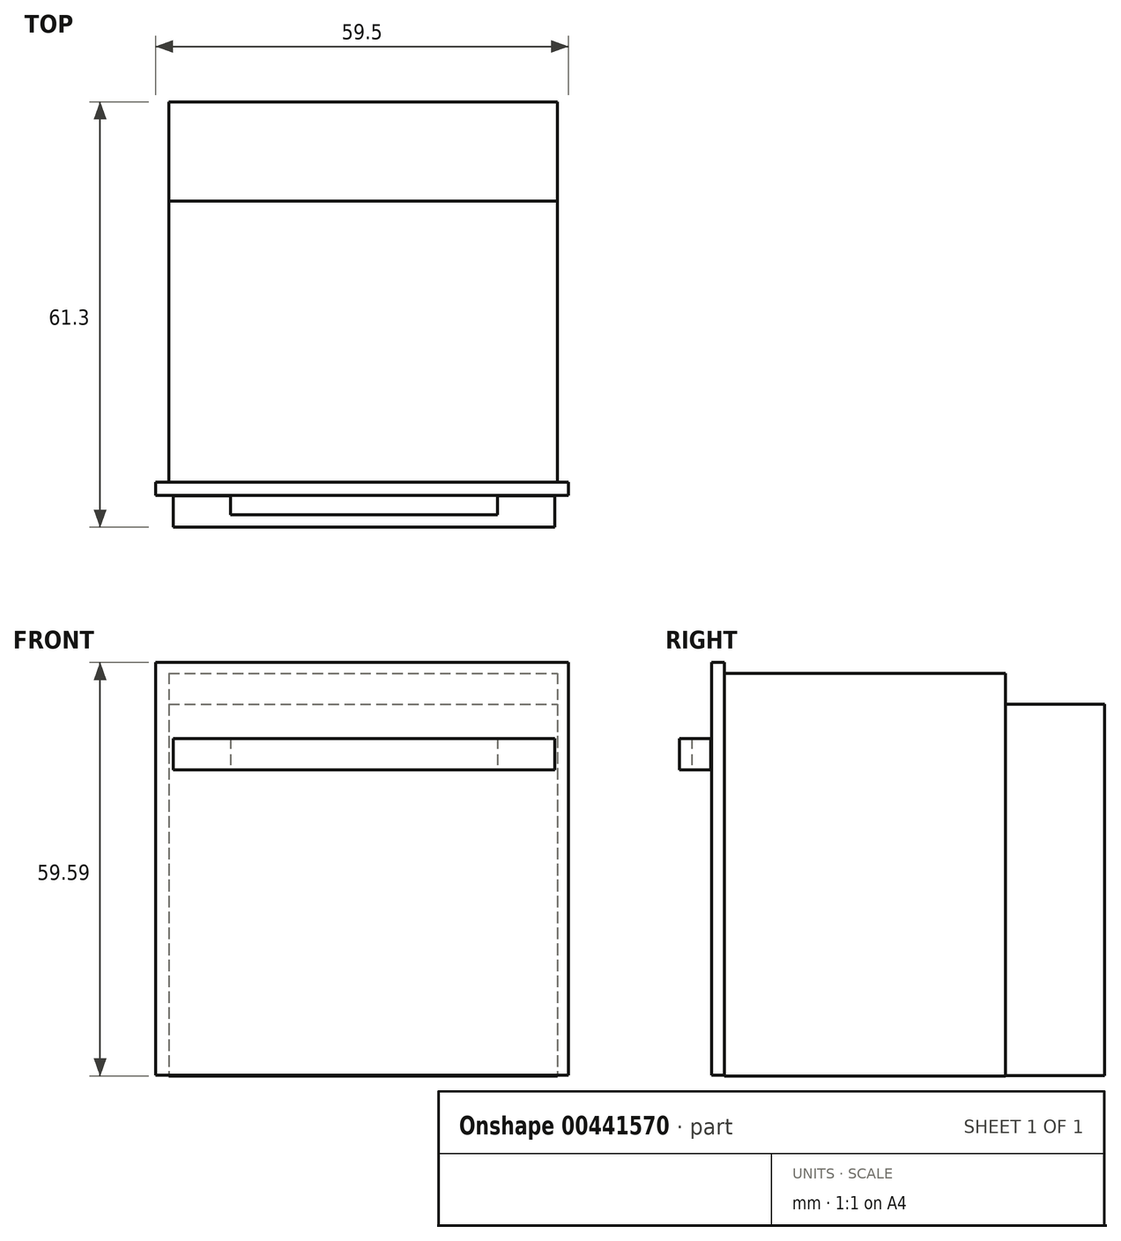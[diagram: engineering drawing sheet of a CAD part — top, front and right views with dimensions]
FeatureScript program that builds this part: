
annotation { "Feature Type Name" : "Feature", "Feature Type Description" : "" }
export const myFeature = defineFeature(function(context is Context, id is Id, definition is map)
    precondition{}
    {
        {
            var Q0;
            Q0=qCreatedBy(makeId("Front.planeOp"),FACE);
            var sketch = newSketch(context, id + "F0", { "sketchPlane" : qUnion([Q0])});
            skLineSegment(sketch, "E0.bottom", {"start": v(-27.15, 28.19) * mm, "end": v(28.85, 28.19) * mm});
            skLineSegment(sketch, "E0.top", {"start": v(-27.15, -29.81) * mm, "end": v(28.85, -29.81) * mm});
            skLineSegment(sketch, "E0.left", {"start": v(-27.15, 28.19) * mm, "end": v(-27.15, -29.81) * mm});
            skLineSegment(sketch, "E0.right", {"start": v(28.85, 28.19) * mm, "end": v(28.85, -29.81) * mm});
            skSolve(sketch);
        }
        {
            var Q0;
            Q0=makeQuery(id+"F0.imprint","IMPRINT",FACE,{"disambiguationData":[TD([[makeQuery(id+"F0.imprint","IMPRINT",EDGE,{"derivedFrom":sQuery(id+"F0.wireOp",EDGE,"E0.bottom")}),-1.0]])]});
            extrude(context, id + "F1", {"entities" : qUnion([Q0]), "depth" : 40.5 * mm});
        }
        {
            var Q0;
            Q0=qCreatedBy(makeId("Front.planeOp"),FACE);
            var sketch = newSketch(context, id + "F2", { "sketchPlane" : qUnion([Q0])});
            skLineSegment(sketch, "E1.bottom", {"start": v(-29.54, 26.56) * mm, "end": v(26.46, 26.56) * mm});
            skLineSegment(sketch, "E1.top", {"start": v(-29.54, -26.94) * mm, "end": v(26.46, -26.94) * mm});
            skLineSegment(sketch, "E1.left", {"start": v(-29.54, 26.56) * mm, "end": v(-29.54, -26.94) * mm});
            skLineSegment(sketch, "E1.right", {"start": v(26.46, 26.56) * mm, "end": v(26.46, -26.94) * mm});
            skSolve(sketch);
        }
        {
            var Q0;
            Q0 = qSketchRegion(id + "F2", true);
            extrude(context, id + "F3", {"entities" : qUnion([Q0]), "depth" : 14.3 * mm});
        }
        {
            var Q0;
            Q0=makeQuery(id+"F3.opExtrude","SWEPT_BODY",BODY,{"disambiguationData":[OSD([sQuery(id+"F2.wireOp",EDGE,"E1.bottom"),sQuery(id+"F2.wireOp",EDGE,"E1.top"),sQuery(id+"F2.wireOp",EDGE,"E1.left"),sQuery(id+"F2.wireOp",EDGE,"E1.right")])]});
            var Q1;
            Q1=makeQuery(id+"F3.opExtrude","CAP_FACE",FACE,{"disambiguationData":[OSD([sQuery(id+"F2.wireOp",EDGE,"E1.bottom"),sQuery(id+"F2.wireOp",EDGE,"E1.top"),sQuery(id+"F2.wireOp",EDGE,"E1.left"),sQuery(id+"F2.wireOp",EDGE,"E1.right")])],"isStart":false});
            transform(context, id + "F4", {"entities" : qUnion([Q0]), "transformType" : TransformType.TRANSLATION_DISTANCE, "transformDirection" : qUnion([Q1]), "distance" : 16.5 * mm, "oppositeDirection" : true, "makeCopy" : false});
        }
        {
            var Q0;
            Q0=makeQuery(id+"F3.opExtrude","SWEPT_BODY",BODY,{"disambiguationData":[OSD([sQuery(id+"F2.wireOp",EDGE,"E1.bottom"),sQuery(id+"F2.wireOp",EDGE,"E1.top"),sQuery(id+"F2.wireOp",EDGE,"E1.left"),sQuery(id+"F2.wireOp",EDGE,"E1.right")])]});
            transform(context, id + "F5", {"entities" : qUnion([Q0]), "transformType" : TransformType.TRANSLATION_3D, "dx" : 2.4 * mm, "dy" : -2.2 * mm, "dz" : -2.8 * mm, "makeCopy" : false});
        }
        {
            var Q0;
            Q0=qCreatedBy(makeId("Front.planeOp"),FACE);
            var sketch = newSketch(context, id + "F6", { "sketchPlane" : qUnion([Q0])});
            skLineSegment(sketch, "E2.bottom", {"start": v(-30.65, 29.85) * mm, "end": v(28.85, 29.85) * mm});
            skLineSegment(sketch, "E2.top", {"start": v(-30.65, -29.65) * mm, "end": v(28.85, -29.65) * mm});
            skLineSegment(sketch, "E2.left", {"start": v(-30.65, 29.85) * mm, "end": v(-30.65, -29.65) * mm});
            skLineSegment(sketch, "E2.right", {"start": v(28.85, 29.85) * mm, "end": v(28.85, -29.65) * mm});
            skSolve(sketch);
        }
        {
            var Q0;
            Q0 = qSketchRegion(id + "F6", true);
            extrude(context, id + "F7", {"entities" : qUnion([Q0]), "depth" : 1.9 * mm});
        }
        {
            var Q0;
            Q0=makeQuery(id+"F7.opExtrude","SWEPT_BODY",BODY,{"disambiguationData":[OSD([sQuery(id+"F6.wireOp",EDGE,"E2.bottom"),sQuery(id+"F6.wireOp",EDGE,"E2.top"),sQuery(id+"F6.wireOp",EDGE,"E2.left"),sQuery(id+"F6.wireOp",EDGE,"E2.right")])]});
            transform(context, id + "F8", {"entities" : qUnion([Q0]), "transformType" : TransformType.TRANSLATION_3D, "dx" : 1.6 * mm, "dy" : -40.5 * mm, "dz" : -0.07 * mm, "makeCopy" : false});
        }
        {
            var Q0;
            Q0=qCreatedBy(makeId("Front.planeOp"),FACE);
            var sketch = newSketch(context, id + "F9", { "sketchPlane" : qUnion([Q0])});
            skLineSegment(sketch, "E3", {"start": v(-40.02, 11.42) * mm, "end": v(-40.02, 6.92) * mm});
            skLineSegment(sketch, "E4", {"start": v(-40.02, 6.92) * mm, "end": v(14.98, 6.92) * mm});
            skLineSegment(sketch, "E5", {"start": v(14.98, 11.42) * mm, "end": v(6.74, 11.42) * mm});
            skLineSegment(sketch, "E6", {"start": v(6.74, 11.42) * mm, "end": v(6.74, 8.71) * mm});
            skLineSegment(sketch, "E7", {"start": v(6.74, 8.71) * mm, "end": v(-31.78, 8.71) * mm});
            skLineSegment(sketch, "E8", {"start": v(-31.78, 8.71) * mm, "end": v(-31.78, 11.42) * mm});
            skLineSegment(sketch, "E9", {"start": v(-31.78, 11.42) * mm, "end": v(-40.02, 11.42) * mm});
            skLineSegment(sketch, "E10", {"start": v(14.98, 11.42) * mm, "end": v(14.98, 6.92) * mm});
            skSolve(sketch);
        }
        {
            var Q0;
            Q0=makeQuery(id+"F9.imprint","IMPRINT",FACE,{"disambiguationData":[TD([[makeQuery(id+"F9.imprint","IMPRINT",EDGE,{"derivedFrom":sQuery(id+"F9.wireOp",EDGE,"E3")}),1.0]])]});
            extrude(context, id + "F10", {"entities" : qUnion([Q0]), "depth" : 4.5 * mm});
        }
        {
            var Q0;
            Q0=makeQuery(id+"F10.opExtrude","SWEPT_BODY",BODY,{"disambiguationData":[OSD([sQuery(id+"F9.wireOp",EDGE,"E3"),sQuery(id+"F9.wireOp",EDGE,"E4"),sQuery(id+"F9.wireOp",EDGE,"E5"),sQuery(id+"F9.wireOp",EDGE,"E6"),sQuery(id+"F9.wireOp",EDGE,"E7"),sQuery(id+"F9.wireOp",EDGE,"E8"),sQuery(id+"F9.wireOp",EDGE,"E9"),sQuery(id+"F9.wireOp",EDGE,"E10")])]});
            var Q1;
            Q1=makeQuery(id+"F10.opExtrude","CAP_EDGE",EDGE,{"disambiguationData":[OSD([sQuery(id+"F9.wireOp",EDGE,"E5")])],"isStart":false});
            transform(context, id + "F11", {"entities" : qUnion([Q0]), "transformType" : TransformType.ROTATION, "transformAxis" : qUnion([Q1]), "angle" : 90 * degree, "makeCopy" : false});
        }
        {
            var Q0;
            Q0=makeQuery(id+"F10.opExtrude","SWEPT_BODY",BODY,{"disambiguationData":[OSD([sQuery(id+"F9.wireOp",EDGE,"E3"),sQuery(id+"F9.wireOp",EDGE,"E4"),sQuery(id+"F9.wireOp",EDGE,"E5"),sQuery(id+"F9.wireOp",EDGE,"E6"),sQuery(id+"F9.wireOp",EDGE,"E7"),sQuery(id+"F9.wireOp",EDGE,"E8"),sQuery(id+"F9.wireOp",EDGE,"E9"),sQuery(id+"F9.wireOp",EDGE,"E10")])]});
            transform(context, id + "F12", {"entities" : qUnion([Q0]), "transformType" : TransformType.TRANSLATION_3D, "dx" : 13.5 * mm, "dy" : -38 * mm, "dz" : 7.4 * mm, "makeCopy" : false});
        }
    });
